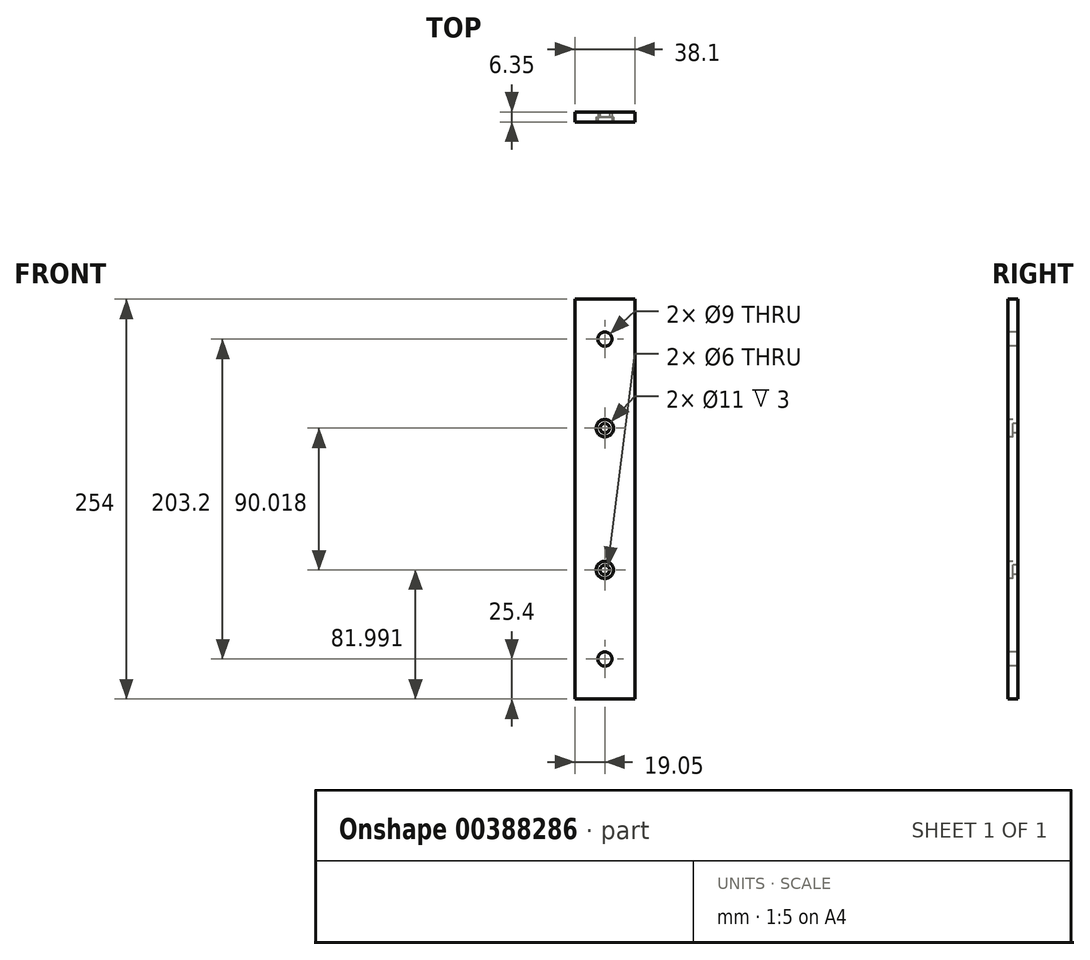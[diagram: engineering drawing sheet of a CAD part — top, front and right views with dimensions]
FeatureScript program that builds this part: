
annotation { "Feature Type Name" : "Feature", "Feature Type Description" : "" }
export const myFeature = defineFeature(function(context is Context, id is Id, definition is map)
    precondition{}
    {
        {
            var Q0;
            Q0=qCreatedBy(makeId("Top.planeOp"),FACE);
            var sketch = newSketch(context, id + "F0", { "sketchPlane" : qUnion([Q0])});
            skLineSegment(sketch, "E0.bottom", {"start": v(0, 0) * mm, "end": v(38.1, 0) * mm});
            skLineSegment(sketch, "E0.top", {"start": v(0, 6.35) * mm, "end": v(38.1, 6.35) * mm});
            skLineSegment(sketch, "E0.left", {"start": v(0, 0) * mm, "end": v(0, 6.35) * mm});
            skLineSegment(sketch, "E0.right", {"start": v(38.1, 0) * mm, "end": v(38.1, 6.35) * mm});
            skSolve(sketch);
        }
        {
            var Q0;
            Q0 = qSketchRegion(id + "F0", true);
            extrude(context, id + "F1", {"entities" : qUnion([Q0]), "depth" : 254 * mm});
        }
        {
            var Q0;
            Q0=makeQuery(id+"F1.opExtrude","SWEPT_FACE",FACE,{"disambiguationData":[OSD([sQuery(id+"F0.wireOp",EDGE,"E0.bottom")])]});
            var sketch = newSketch(context, id + "F2", { "sketchPlane" : qUnion([Q0])});
            skLineSegment(sketch, "E1", {"start": v(19.05, 254) * mm, "end": v(19.05, 0) * mm, "construction": true});
            skPoint(sketch, "E2", {"position": v(19.05, 172) * mm});
            skPoint(sketch, "E3", {"position": v(19.05, 25.4) * mm});
            skPoint(sketch, "E4", {"position": v(19.05, 228.6) * mm});
            skPoint(sketch, "E5", {"position": v(19.05, 82) * mm});
            skSolve(sketch);
        }
        {
            var Q0;
            Q0=sQuery(id+"F2.wireOp",VERTEX,"E3");
            var Q1;
            Q1=sQuery(id+"F2.wireOp",VERTEX,"E4");
            var Q2;
            Q2=makeQuery(id+"F1.opExtrude","SWEPT_BODY",BODY,{"disambiguationData":[OSD([sQuery(id+"F0.wireOp",EDGE,"E0.bottom"),sQuery(id+"F0.wireOp",EDGE,"E0.top"),sQuery(id+"F0.wireOp",EDGE,"E0.left"),sQuery(id+"F0.wireOp",EDGE,"E0.right")])]});
            hole(context, id + "F3", {"style" : HoleStyle.SIMPLE, "endStyle" : HoleEndStyle.THROUGH, "holeDiameter" : 9 * mm, "isTappedThrough" : true, "tappedDepth" : 12.7 * mm, "tapClearance" : 3, "locations" : qUnion([Q0, Q1]), "scope" : qUnion([Q2])});
        }
        {
            var Q0;
            Q0=sQuery(id+"F2.wireOp",VERTEX,"E2");
            var Q1;
            Q1=sQuery(id+"F2.wireOp",VERTEX,"E5");
            var Q2;
            Q2=makeQuery(id+"F1.opExtrude","SWEPT_BODY",BODY,{"disambiguationData":[OSD([sQuery(id+"F0.wireOp",EDGE,"E0.bottom"),sQuery(id+"F0.wireOp",EDGE,"E0.top"),sQuery(id+"F0.wireOp",EDGE,"E0.left"),sQuery(id+"F0.wireOp",EDGE,"E0.right")])]});
            hole(context, id + "F4", {"style" : HoleStyle.C_BORE, "endStyle" : HoleEndStyle.THROUGH, "holeDiameter" : 6 * mm, "cBoreDiameter" : 11 * mm, "cBoreDepth" : 3 * mm, "isTappedThrough" : true, "tappedDepth" : 12.7 * mm, "tapClearance" : 3, "locations" : qUnion([Q0, Q1]), "scope" : qUnion([Q2])});
        }
    });
